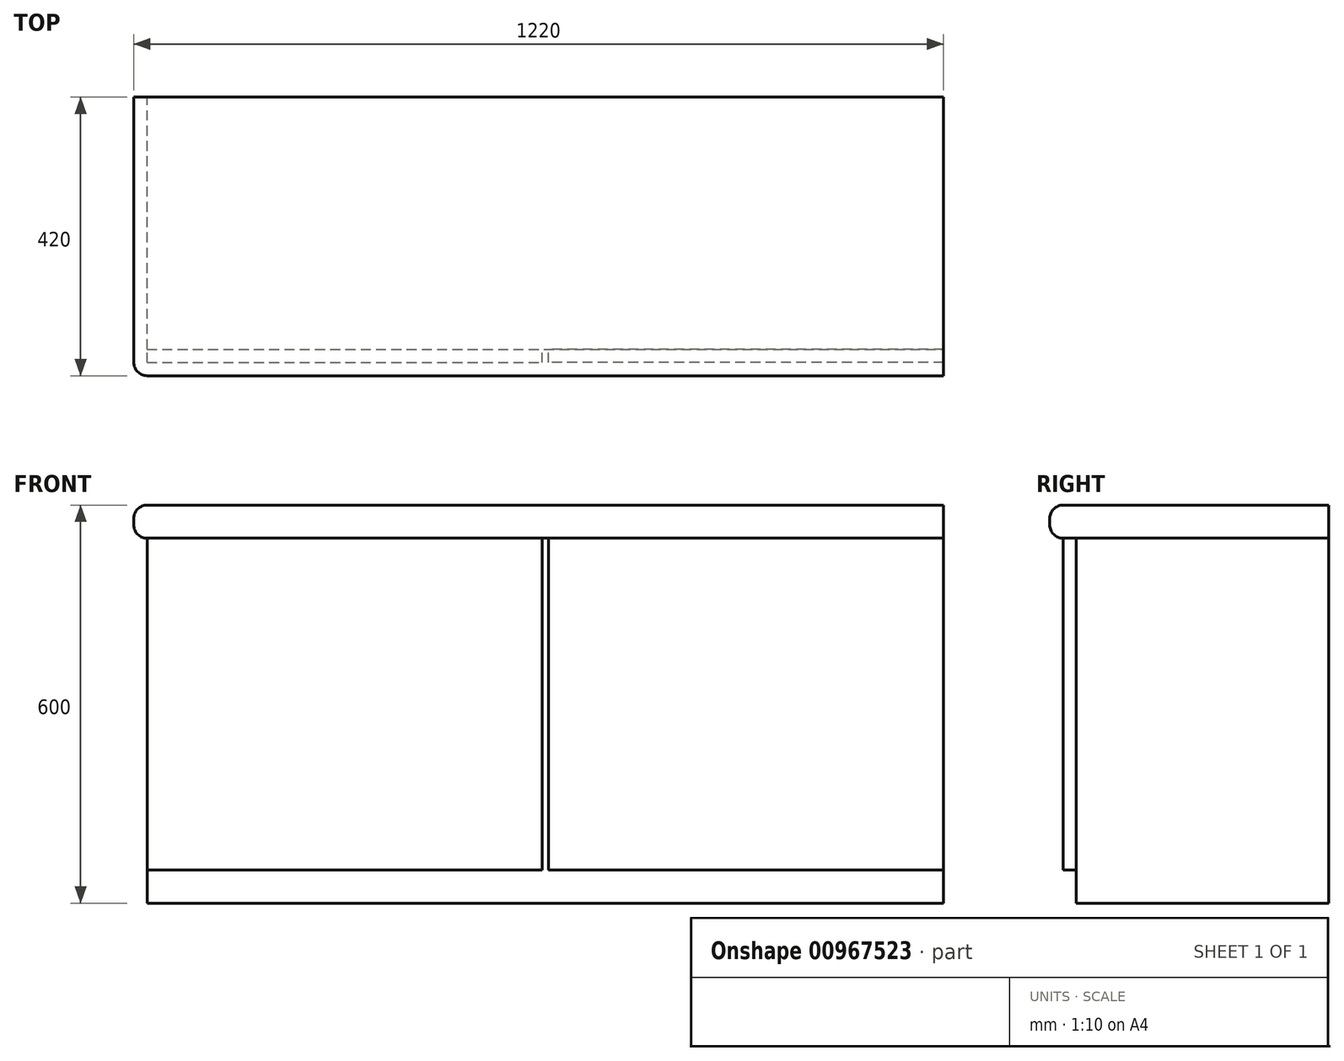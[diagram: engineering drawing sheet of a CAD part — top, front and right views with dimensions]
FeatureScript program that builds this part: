
annotation { "Feature Type Name" : "Feature", "Feature Type Description" : "" }
export const myFeature = defineFeature(function(context is Context, id is Id, definition is map)
    precondition{}
    {
        {
            assignVariable(context, id + "F0", {"variableType" : VariableType.LENGTH, "name" : "H", "lengthValue" : 600 * mm});
        }
        {
            var Q0;
            Q0=qCreatedBy(makeId("Top.planeOp"),FACE);
            var sketch = newSketch(context, id + "F1", { "sketchPlane" : qUnion([Q0])});
            skLineSegment(sketch, "E0.bottom", {"start": v(0, 0) * mm, "end": v(1200, 0) * mm});
            skLineSegment(sketch, "E0.top", {"start": v(0, 380) * mm, "end": v(1200, 380) * mm});
            skLineSegment(sketch, "E0.left", {"start": v(0, 0) * mm, "end": v(0, 380) * mm});
            skLineSegment(sketch, "E0.right", {"start": v(1200, 0) * mm, "end": v(1200, 380) * mm});
            skSolve(sketch);
        }
        {
            var Q0;
            Q0 = qSketchRegion(id + "F1", true);
            extrude(context, id + "F2", {"entities" : qUnion([Q0]), "depth" : getVariable(context, 'H') - 50 * mm, "offsetDistance" : 25 * mm});
        }
        {
            var Q0;
            Q0=makeQuery(id+"F2.opExtrude","SWEPT_FACE",FACE,{"disambiguationData":[OSD([sQuery(id+"F1.wireOp",EDGE,"E0.bottom")])]});
            var sketch = newSketch(context, id + "F3", { "sketchPlane" : qUnion([Q0])});
            skLineSegment(sketch, "E1.bottom", {"start": v(0, 550) * mm, "end": v(595, 550) * mm});
            skLineSegment(sketch, "E1.top", {"start": v(0, 50) * mm, "end": v(595, 50) * mm});
            skLineSegment(sketch, "E1.left", {"start": v(0, 550) * mm, "end": v(0, 50) * mm});
            skLineSegment(sketch, "E1.right", {"start": v(595, 550) * mm, "end": v(595, 50) * mm});
            skLineSegment(sketch, "E2.bottom", {"start": v(1200, 550) * mm, "end": v(605, 550) * mm});
            skLineSegment(sketch, "E2.top", {"start": v(1200, 50) * mm, "end": v(605, 50) * mm});
            skLineSegment(sketch, "E2.left", {"start": v(1200, 550) * mm, "end": v(1200, 50) * mm});
            skLineSegment(sketch, "E2.right", {"start": v(605, 550) * mm, "end": v(605, 50) * mm});
            skSolve(sketch);
        }
        {
            var Q0;
            Q0 = qSketchRegion(id + "F3", true);
            extrude(context, id + "F4", {"entities" : qUnion([Q0]), "depth" : 20 * mm, "offsetDistance" : 25 * mm});
        }
        {
            var Q0;
            Q0=makeQuery(id+"F2.opExtrude","SWEPT_FACE",FACE,{"disambiguationData":[OSD([sQuery(id+"F1.wireOp",EDGE,"E0.right")])]});
            var sketch = newSketch(context, id + "F5", { "sketchPlane" : qUnion([Q0])});
            skLineSegment(sketch, "E3.bottom", {"start": v(380, 550) * mm, "end": v(-40, 550) * mm});
            skLineSegment(sketch, "E3.top", {"start": v(380, 600) * mm, "end": v(-40, 600) * mm});
            skLineSegment(sketch, "E3.left", {"start": v(380, 550) * mm, "end": v(380, 600) * mm});
            skLineSegment(sketch, "E3.right", {"start": v(-40, 550) * mm, "end": v(-40, 600) * mm});
            skSolve(sketch);
        }
        {
            var Q0;
            Q0 = qSketchRegion(id + "F5", true);
            var Q1;
            Q1=makeQuery(id+"F2.opExtrude","SWEPT_FACE",FACE,{"disambiguationData":[OSD([sQuery(id+"F1.wireOp",EDGE,"E0.left")])]});
            extrude(context, id + "F6", {"entities" : qUnion([Q0]), "endBound" : BoundingType.UP_TO_SURFACE, "oppositeDirection" : true, "depth" : 25 * mm, "endBoundEntityFace" : qUnion([Q1]), "hasOffset" : true, "offsetDistance" : 20 * mm, "offsetOppositeDirection" : true});
        }
        {
            var Q0;
            Q0=makeQuery(id+"F6.opExtrude","SWEPT_EDGE",EDGE,{"disambiguationData":[OSD([sQuery(id+"F5.wireOp",EDGE,"E3.top"),sQuery(id+"F5.wireOp",EDGE,"E3.right")])]});
            var Q1;
            Q1=makeQuery(id+"F6.opExtrude","CAP_EDGE",EDGE,{"disambiguationData":[OSD([sQuery(id+"F5.wireOp",EDGE,"E3.top")])],"isStart":false});
            var Q2;
            Q2=makeQuery(id+"F6.opExtrude","CAP_EDGE",EDGE,{"disambiguationData":[OSD([sQuery(id+"F5.wireOp",EDGE,"E3.bottom")])],"isStart":false});
            var Q3;
            Q3=makeQuery(id+"F6.opExtrude","CAP_EDGE",EDGE,{"disambiguationData":[OSD([sQuery(id+"F5.wireOp",EDGE,"E3.right")])],"isStart":false});
            var Q4;
            Q4=makeQuery(id+"F6.opExtrude","SWEPT_EDGE",EDGE,{"disambiguationData":[OSD([sQuery(id+"F5.wireOp",EDGE,"E3.bottom"),sQuery(id+"F5.wireOp",EDGE,"E3.right")])]});
            fillet(context, id + "F7", {"entities" : qUnion([Q0, Q1, Q2, Q3, Q4]), "tangentPropagation" : true, "radius" : 20 * mm, "defaultsChanged" : true, "vertexSettings" : [], "allowEdgeOverflow" : false});
        }
    });
